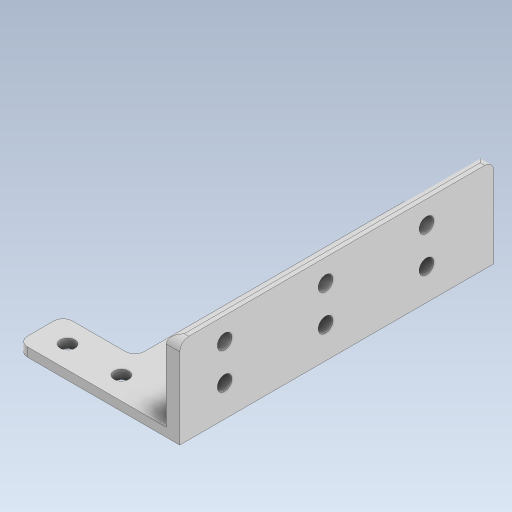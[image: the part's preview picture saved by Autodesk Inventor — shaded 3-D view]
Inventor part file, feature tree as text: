
AUTODESK INVENTOR PART (.ipt)
format: ipt  version: 2023.5 (Build 275446000, 446)  size: 351,744 bytes
history: native  units: mm
features: extrude x3, sketch x2, fillet x1
ambient origin geometry x8: Origin, YZ Plane, XZ Plane, XY Plane, X Axis, Y Axis, Z Axis, Center Point
bodies: Solid1 (feature_tree)
feature tree (6):
  sketch  "Sketch1"  dims[d0=3.3mm d1=3.3mm]
  extrude  "Extrusion1"  Depth=3.3mm
  extrude  "Extrusion2"  Depth=2.0mm
  extrude  "Extrusion3"  Depth=2.0mm
  fillet  "Fillet1"  Radius=20.0mm
  sketch  "Sketch2"  dims[d2=12.0mm d3=3.3mm d4=12.5mm d5=20.0mm d6=3.3mm d7=40.0mm d8=20.0mm d9=35.0mm d10=2.0mm d11=0.0mm d12=20.0mm d13=0.0mm d14=3.3mm d15=10.0mm d16=3.3mm d18=3.3mm d19=20.0mm d20=0.0mm d21=5.0mm d22=5.0mm d23=5.0mm d24=15.0mm d25=3.3mm d26=20.0mm d27=3.3mm d28=40.0mm d29=2.0mm]
